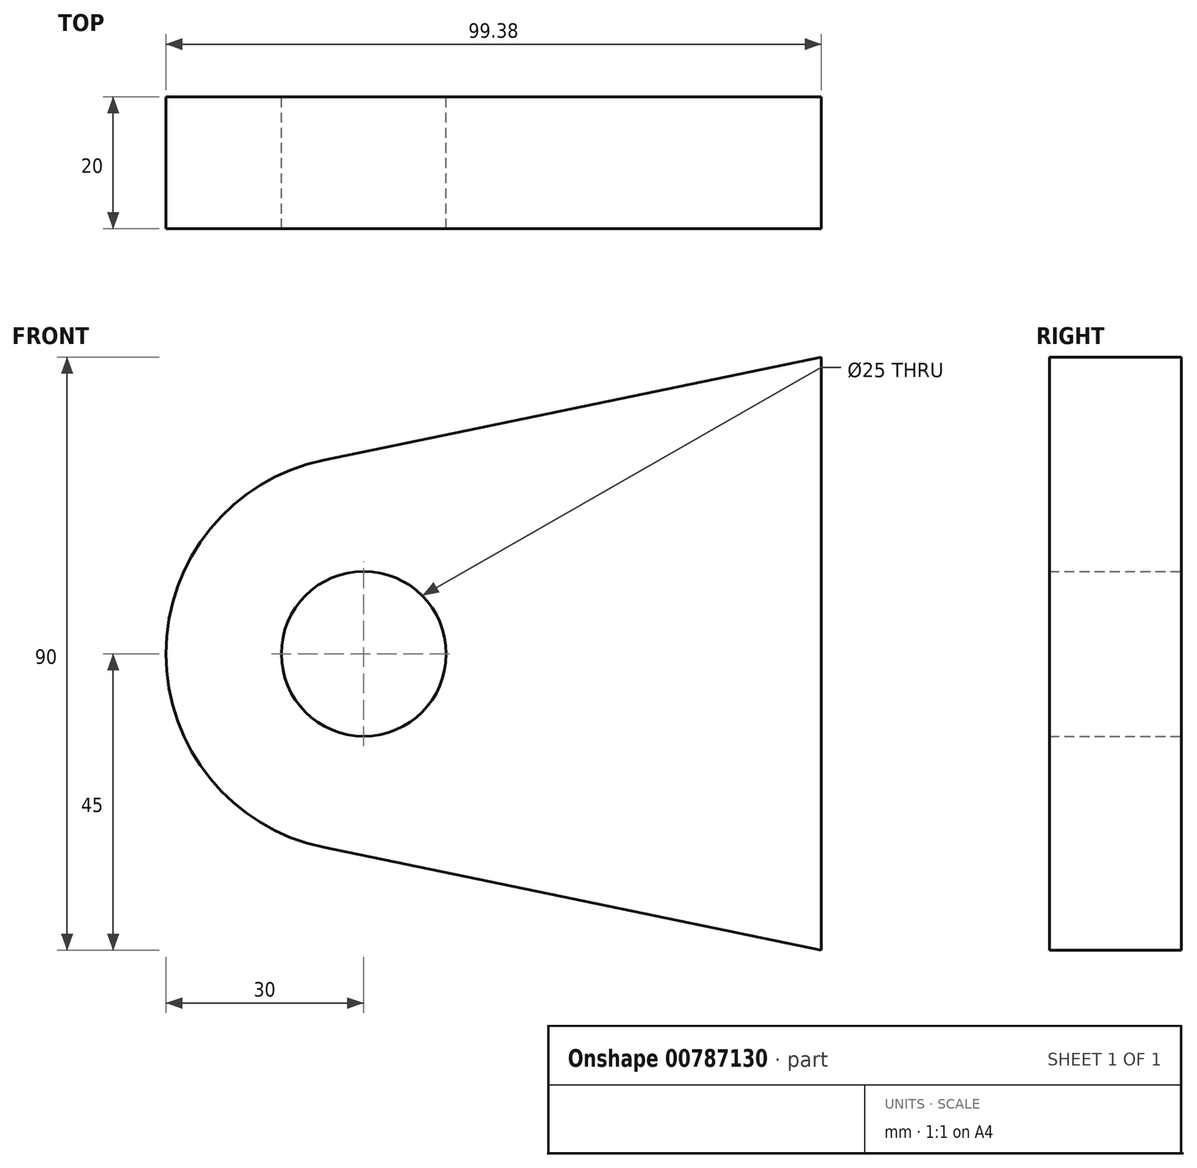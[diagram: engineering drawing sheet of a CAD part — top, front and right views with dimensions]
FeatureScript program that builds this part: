
annotation { "Feature Type Name" : "Feature", "Feature Type Description" : "" }
export const myFeature = defineFeature(function(context is Context, id is Id, definition is map)
    precondition{}
    {
        {
            var Q0;
            Q0=qCreatedBy(makeId("Front.planeOp"),FACE);
            var sketch = newSketch(context, id + "F0", { "sketchPlane" : qUnion([Q0])});
            skLineSegment(sketch, "E0", {"start": v(-0.62, 45) * mm, "end": v(-76.08, 29.38) * mm});
            skLineSegment(sketch, "E1", {"start": v(-0.62, 45) * mm, "end": v(-0.62, -45) * mm});
            skLineSegment(sketch, "E2.MirrorCS", {"start": v(-0.62, -45) * mm, "end": v(-76.08, -29.38) * mm});
            skLineSegment(sketch, "E3", {"start": v(0, 0) * mm, "end": v(-70, 0) * mm, "construction": true});
            skCircle(sketch, "E4", {"center": v(-70, 0) * mm, "radius": 30 * mm});
            skCircle(sketch, "E5", {"center": v(-70, 0) * mm, "radius": 12.5 * mm});
            skSolve(sketch);
        }
        {
            var Q0;
            Q0=makeQuery(id+"F0.imprint","IMPRINT",FACE,{"disambiguationData":[TD([[makeQuery(id+"F0.imprint","IMPRINT",EDGE,{"derivedFrom":sQuery(id+"F0.wireOp",EDGE,"rEyC0sFe-LgNe-Msjr-4Dgy-o0PoiasKttEn")}),-1.0]])]});
            var Q1;
            {var subQ0=sQuery(id+"F0.wireOp",EDGE,"E0");Q1=makeQuery(id+"F0.imprint","IMPRINT",FACE,{"disambiguationData":[TD([[makeQuery(id+"F0.imprint","IMPRINT",EDGE,{"derivedFrom":subQ0}),1.0]])]});}
            extrude(context, id + "F1", {"entities" : qUnion([Q0, Q1]), "depth" : 20 * mm, "offsetDistance" : 25 * mm});
        }
        {
            var Q0;
            Q0=makeQuery(id+"F0.imprint","IMPRINT",FACE,{"disambiguationData":[TD([[makeQuery(id+"F0.imprint","IMPRINT",EDGE,{"derivedFrom":sQuery(id+"F0.wireOp",EDGE,"E5")}),-1.0]])]});
            extrude(context, id + "F2", {"entities" : qUnion([Q0]), "operationType" : NewBodyOperationType.ADD, "depth" : 20 * mm, "offsetDistance" : 25 * mm});
        }
    });
